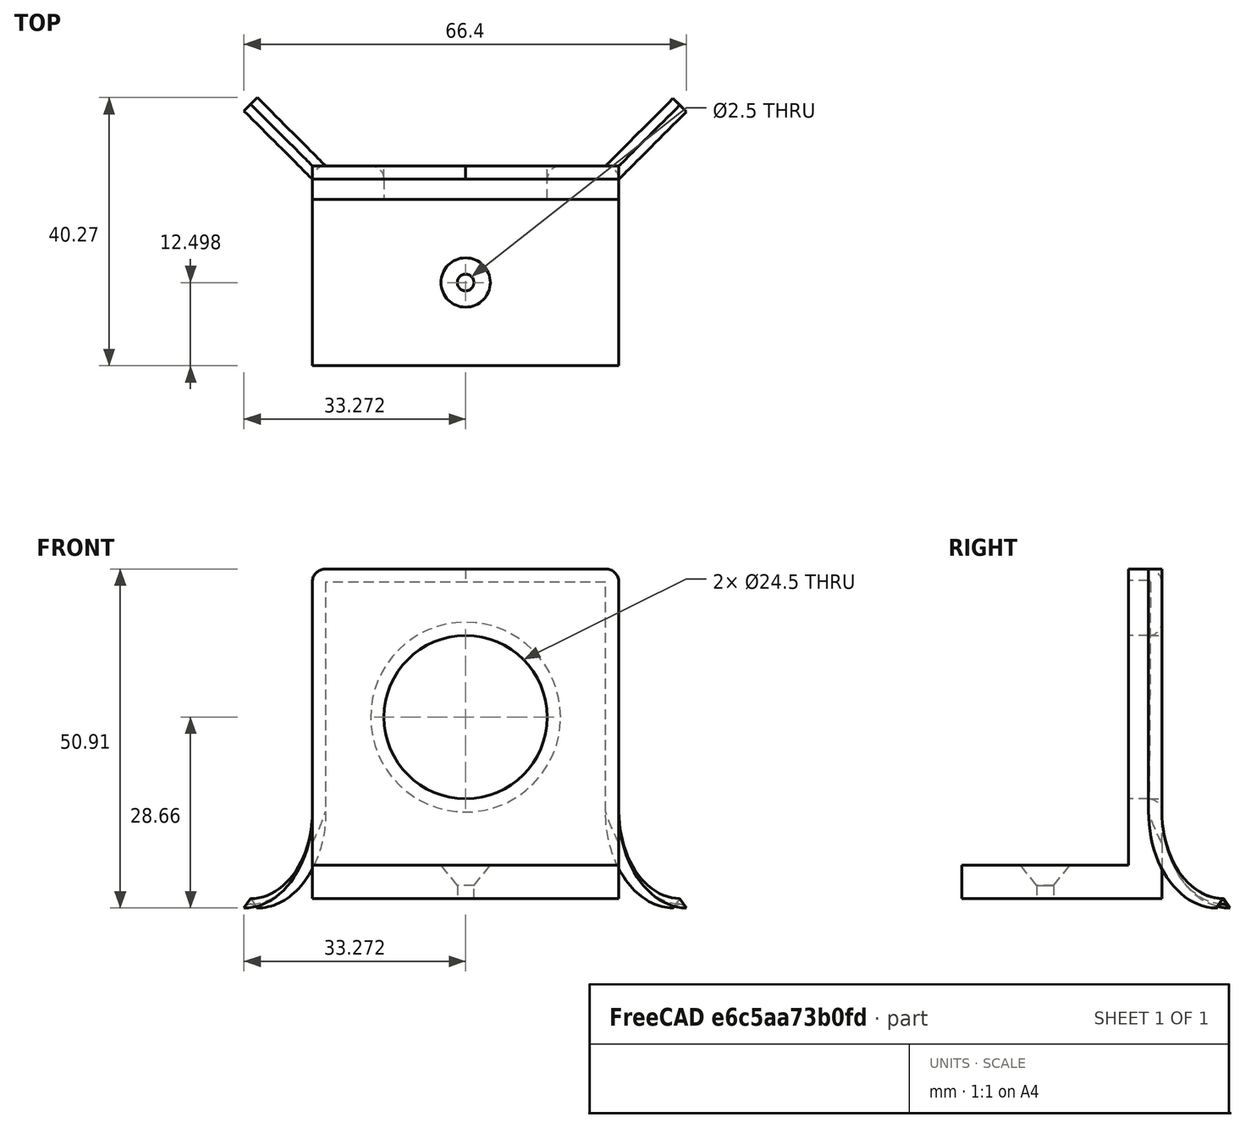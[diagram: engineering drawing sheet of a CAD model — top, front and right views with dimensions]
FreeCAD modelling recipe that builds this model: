
FCSTD DOCUMENT  (FreeCAD 0.18.4R)
Label: Tubus.Tarto
License: All rights reserved
LicenseURL: http://en.wikipedia.org/wiki/All_rights_reserved
objects: Part::Cut×10, Part::Part2DObjectPython×8, Part::Feature×7, Part::Extrusion×4, PartDesign::FeatureBase×3, PartDesign::ShapeBinder×3, PartDesign::AdditivePipe×3, PartDesign::Body×3, Part::MultiFuse×1
note: 45 computed .brp shape members not serialized (recipe doc carries the construction recipe); baked Part::Feature solids carry a one-line shape summary decoded from their .brp

FEATURE [Part::Extrusion] Extrusion013
  Dir = (-46,0,0)
  DirMode = 0
  FaceMakerClass = Part::FaceMakerBullseye
  LengthFwd = 0
  LengthRev = 0
  Solid = true
  Symmetric = false
FEATURE [Part::MultiFuse] Fusion001
  Placement = pos=(-33.558,0.225639,12) rot=(0,0,1;0rad)
FEATURE [Part::Cut] Cut
  Base = -> Extrusion013
  Tool = -> Fusion001
FEATURE [Part::Part2DObjectPython] Circle  # Draft 2D object (typed FeaturePython)
  FirstAngle = 0
  LastAngle = 0
  MakeFace = true
  Placement = pos=(-148.148,-529.302,21.25) rot=(1,0,0;1.5708rad)
  Radius = 12.25
  Support = -> [Cut]
FEATURE [Part::Extrusion] Extrusion
  Base = -> Circle
  Dir = (0,5,-1.1e-15)
  DirMode = 0
  FaceMakerClass = Part::FaceMakerBullseye
  LengthFwd = 0
  LengthRev = 0
  Solid = true
  Symmetric = false
FEATURE [Part::Cut] Cut001
  Base = -> Cut
  Tool = -> Extrusion
FEATURE [Part::Feature] Wire
  shape: bbox 32.14 x 9.142 x 49.5 mm, 0 faces, 0 solids (baked)
FEATURE [Part::Feature] Wire001
  shape: bbox 32.27 x 9.271 x 49.5 mm, 0 faces, 0 solids (baked)
FEATURE [Part::Part2DObjectPython] Rectangle002  # Draft 2D object (typed FeaturePython)
  ChamferSize = 0
  Columns = 1
  FilletRadius = 0
  Height = 2
  Length = 2
  MakeFace = true
  Placement = pos=(-171.148,-524.302,41.5) rot=(0.57735,-0.57735,-0.57735;2.0944rad)
  Rows = 1
  Support = -> [Cut001]
FEATURE [Part::Part2DObjectPython] Circle003  # Draft 2D object (typed FeaturePython)
  FirstAngle = 0
  LastAngle = 0
  MakeFace = true
  Placement = pos=(-171.148,-526.302,41.5) rot=(0.57735,-0.57735,-0.57735;2.0944rad)
  Radius = 2
FEATURE [Part::Cut] Cut002
  Base = -> Rectangle002
  Placement = pos=(23,0,0) rot=(0,0,1;0rad)
  Tool = -> Circle003
FEATURE [Part::Cut] Cut003
  Base = -> Rectangle002
  Placement = pos=(23,0,0) rot=(0,0,1;0rad)
  Tool = -> Circle003
FEATURE [PartDesign::FeatureBase] BaseFeature
  BaseFeature = -> Cut002
FEATURE [PartDesign::ShapeBinder] CopyWire001
  TraceSupport = false
FEATURE [PartDesign::AdditivePipe] AdditivePipe
  AuxilleryCurvelinear = true
  AuxillerySpineTangent = false
  BaseFeature = -> BaseFeature
  Binormal = (0,0,0)
  Mode = 0
  Profile = -> Cut003 [Face1]
  Spine = -> CopyWire001
  SpineTangent = false
  Transformation = 0
  Transition = 0
FEATURE [PartDesign::Body] Body
  BaseFeature = -> Cut002
  Group = -> [BaseFeature,AdditivePipe,CopyWire001]
  Origin = -> Origin
  Tip = -> AdditivePipe
FEATURE [Part::Feature] AdditivePipe001
  shape: bbox 33.68 x 14.62 x 53.64 mm, 12 faces (baked)
FEATURE [PartDesign::FeatureBase] BaseFeature001
  BaseFeature = -> Cut003
FEATURE [PartDesign::ShapeBinder] CopyWire
  TraceSupport = false
FEATURE [PartDesign::AdditivePipe] AdditivePipe002
  AuxilleryCurvelinear = true
  AuxillerySpineTangent = false
  BaseFeature = -> BaseFeature001
  Binormal = (0,0,0)
  Mode = 0
  Profile = -> Cut003 [Face1]
  Spine = -> CopyWire
  SpineTangent = false
  Transformation = 0
  Transition = 0
FEATURE [PartDesign::Body] Body001
  BaseFeature = -> Cut003
  Group = -> [BaseFeature001,AdditivePipe002,CopyWire]
  Origin = -> Origin001
  Tip = -> AdditivePipe002
FEATURE [Part::Feature] AdditivePipe002001  label="AdditivePipe003"
  shape: bbox 33.53 x 14.48 x 53.64 mm, 12 faces (baked)
FEATURE [Part::Cut] Cut004
  Base = -> Cut001
  Tool = -> AdditivePipe001
FEATURE [Part::Cut] Cut005
  Base = -> Cut004
  Tool = -> AdditivePipe002001
FEATURE [Part::Feature] Face
  shape: bbox 2 x 2e-07 x 2 mm, 1 faces, 0 solids (baked)
FEATURE [Part::Extrusion] Extrusion014
  Base = -> Face
  Dir = (0,-5,0)
  DirMode = 0
  FaceMakerClass = Part::FaceMakerBullseye
  LengthFwd = 0
  LengthRev = 0
  Solid = true
  Symmetric = false
FEATURE [Part::Cut] Cut006
  Base = -> Cut005
  Tool = -> Extrusion014
FEATURE [Part::Feature] Face001
  shape: bbox 1.984 x 2e-07 x 1.711 mm, 1 faces, 0 solids (baked)
FEATURE [Part::Extrusion] Extrusion015
  Base = -> Face001
  Dir = (0,-5,0)
  DirMode = 0
  FaceMakerClass = Part::FaceMakerBullseye
  LengthFwd = 0
  LengthRev = 0
  Solid = true
  Symmetric = false
FEATURE [Part::Cut] Cut007  label="Tubus.Tarto"
  Base = -> Cut006
  Tool = -> Extrusion015
FEATURE [Part::Part2DObjectPython] Rectangle  # Draft 2D object (typed FeaturePython)
  ChamferSize = 0
  Columns = 1
  FilletRadius = 0
  Height = 4.13872
  Length = 35.6226
  MakeFace = true
  Placement = pos=(-135.898,-528.441,21.25) rot=(0,0,1;0rad)
  Rows = 1
  Support = -> [Cut007]
FEATURE [Part::Part2DObjectPython] Rectangle003  # Draft 2D object (typed FeaturePython)
  ChamferSize = 0
  Columns = 1
  FilletRadius = 0
  Height = 2
  Length = 2
  MakeFace = true
  Placement = pos=(-135.898,-526.302,21.25) rot=(0,0,1;0rad)
  Rows = 1
  Support = -> [Cut007]
FEATURE [Part::Part2DObjectPython] Circle004  # Draft 2D object (typed FeaturePython)
  FirstAngle = 0
  LastAngle = 0
  MakeFace = true
  Placement = pos=(-133.898,-526.302,21.25) rot=(0,0,1;0rad)
  Radius = 2
  Support = -> [Rectangle]
FEATURE [Part::Cut] Cut008
  Base = -> Rectangle003
  Tool = -> Circle004
FEATURE [Part::Part2DObjectPython] Line  # Draft 2D object (typed FeaturePython)
  ChamferSize = 0
  Closed = false
  End = (-135.898,-524.302,21.25)
  FilletRadius = 0
  Length = 24.5
  MakeFace = true
  Placement = pos=(-160.398,-524.302,21.25) rot=(-1,0,0;1.5708rad)
  Points = (2) [(0,0,0),(24.5,-1.42109e-14,0)]
  Start = (-160.398,-524.302,21.25)
  Subdivisions = 0
  Support = -> [Cut007]
FEATURE [Part::Part2DObjectPython] Arc  # Draft 2D object (typed FeaturePython)
  FirstAngle = 0
  LastAngle = 360
  MakeFace = true
  Placement = pos=(-148.148,-524.302,21.25) rot=(-1,0,0;1.5708rad)
  Radius = 12.25
  Support = -> [Cut007]
FEATURE [PartDesign::FeatureBase] BaseFeature002
  BaseFeature = -> Cut008
FEATURE [PartDesign::ShapeBinder] CopyArc
  Placement = pos=(-148.148,-524.302,21.25) rot=(-1,0,0;1.5708rad)
  TraceSupport = false
FEATURE [PartDesign::AdditivePipe] AdditivePipe002002
  AuxilleryCurvelinear = true
  AuxillerySpineTangent = false
  BaseFeature = -> BaseFeature002
  Binormal = (0,0,0)
  Mode = 0
  Profile = -> BaseFeature002 [Face1]
  Spine = -> CopyArc [Edge1]
  SpineTangent = false
  Transformation = 0
  Transition = 0
FEATURE [PartDesign::Body] Body002
  BaseFeature = -> Cut008
  Group = -> [BaseFeature002,AdditivePipe002002,CopyArc]
  Origin = -> Origin002
  Tip = -> AdditivePipe002002
FEATURE [Part::Feature] AdditivePipe002002001  label="AdditivePipe002003"
  shape: bbox 33.92 x 3.42 x 33.92 mm, 3 faces (baked)
FEATURE [Part::Cut] Cut009  label="Tubus.Tarto001"
  Base = -> Cut007
  Tool = -> AdditivePipe002002001
